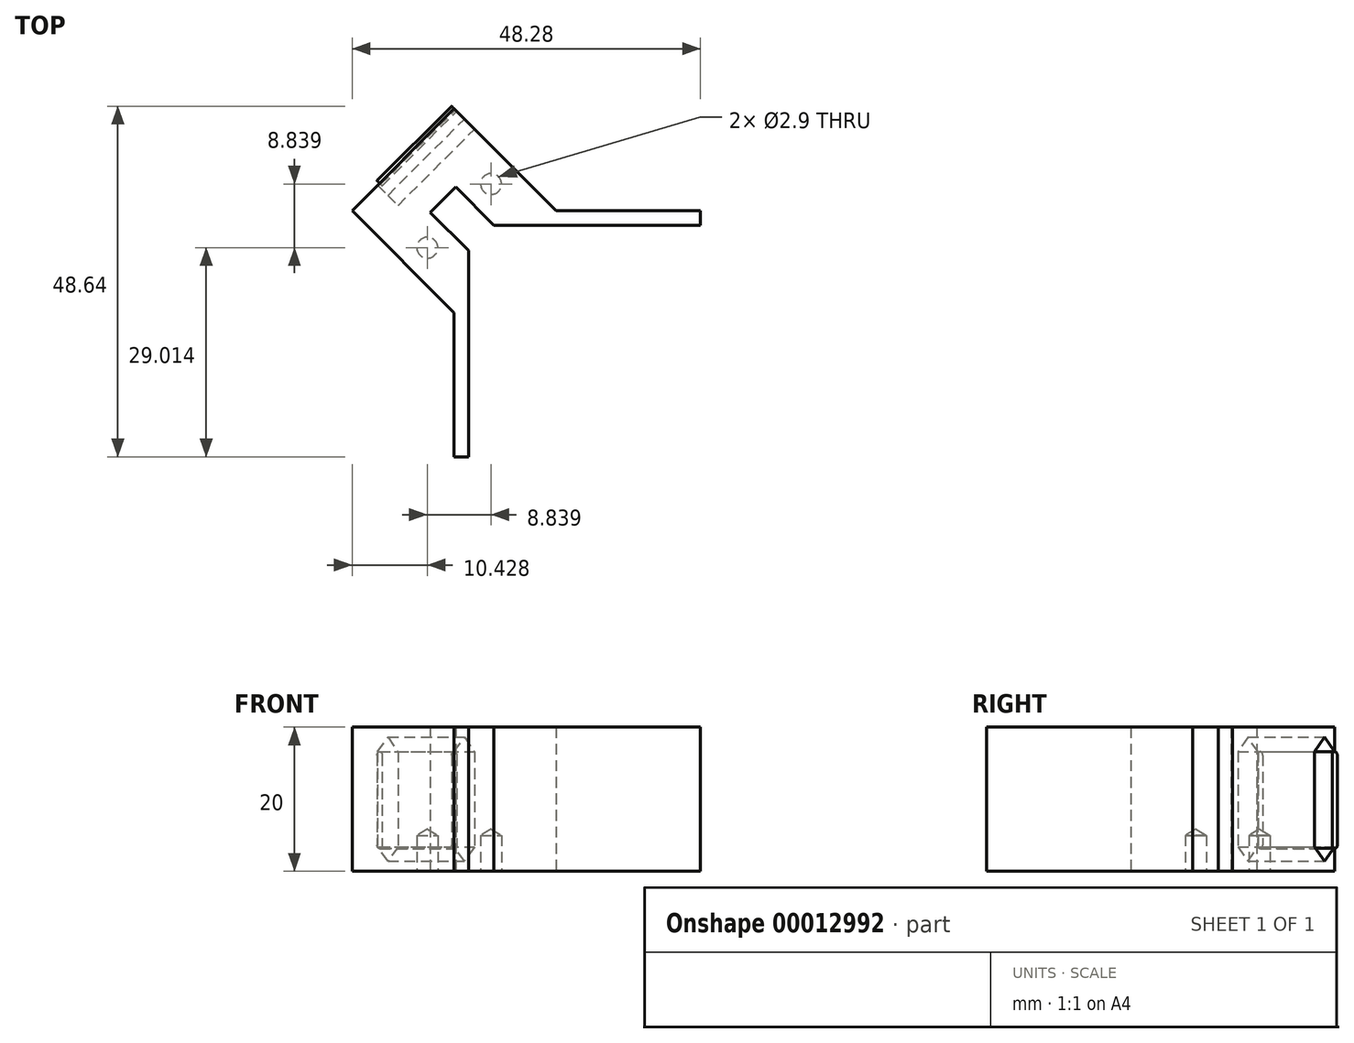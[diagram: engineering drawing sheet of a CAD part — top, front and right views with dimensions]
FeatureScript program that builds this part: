
annotation { "Feature Type Name" : "Feature", "Feature Type Description" : "" }
export const myFeature = defineFeature(function(context is Context, id is Id, definition is map)
    precondition{}
    {
        {
            var Q0;
            Q0=qCreatedBy(makeId("Top.planeOp"),FACE);
            var sketch = newSketch(context, id + "F0", { "sketchPlane" : qUnion([Q0])});
            skLineSegment(sketch, "E0", {"start": v(-14.14, 0) * mm, "end": v(0, -14.14) * mm});
            skLineSegment(sketch, "E1", {"start": v(0, -14.14) * mm, "end": v(0, -34.14) * mm});
            skLineSegment(sketch, "E2", {"start": v(0, -34.14) * mm, "end": v(2, -34.14) * mm});
            skLineSegment(sketch, "E3", {"start": v(2, -34.14) * mm, "end": v(2, -5.54) * mm});
            skLineSegment(sketch, "E4", {"start": v(2, -5.54) * mm, "end": v(-3.3, -0.23) * mm});
            skLineSegment(sketch, "E5", {"start": v(-3.3, -0.23) * mm, "end": v(0.23, 3.3) * mm});
            skLineSegment(sketch, "E6", {"start": v(0.23, 3.3) * mm, "end": v(5.54, -2) * mm});
            skLineSegment(sketch, "E7", {"start": v(5.54, -2) * mm, "end": v(34.14, -2) * mm});
            skLineSegment(sketch, "E8", {"start": v(34.14, -2) * mm, "end": v(34.14, 0) * mm});
            skLineSegment(sketch, "E9", {"start": v(0, 14.14) * mm, "end": v(14.14, 0) * mm});
            skLineSegment(sketch, "E10", {"start": v(14.14, 0) * mm, "end": v(34.14, 0) * mm});
            skLineSegment(sketch, "E11", {"start": v(-14.14, 0) * mm, "end": v(0, 14.14) * mm});
            skSolve(sketch);
        }
        {
            var Q0;
            Q0=makeQuery(id+"F0.imprint","IMPRINT",FACE,{"disambiguationData":[TD([[makeQuery(id+"F0.imprint","IMPRINT",EDGE,{"derivedFrom":sQuery(id+"F0.wireOp",EDGE,"E0")}),1.0]])]});
            extrude(context, id + "F1", {"entities" : qUnion([Q0]), "depth" : 20 * mm});
        }
        {
            var Q0;
            Q0=makeQuery(id+"F1.opExtrude","SWEPT_FACE",FACE,{"disambiguationData":[OSD([sQuery(id+"F0.wireOp",EDGE,"E9")])]});
            var sketch = newSketch(context, id + "F2", { "sketchPlane" : qUnion([Q0])});
            skLineSegment(sketch, "E12.bottom", {"start": v(10, 1.4) * mm, "end": v(6, 1.4) * mm, "construction": true});
            skLineSegment(sketch, "E12.top", {"start": v(10, 18.6) * mm, "end": v(6, 18.6) * mm, "construction": true});
            skLineSegment(sketch, "E12.left", {"start": v(10, 1.4) * mm, "end": v(10, 18.6) * mm, "construction": true});
            skLineSegment(sketch, "E12.right", {"start": v(6, 1.4) * mm, "end": v(6, 18.6) * mm, "construction": true});
            skLineSegment(sketch, "E13", {"start": v(10, 16.6) * mm, "end": v(8, 18.6) * mm});
            skLineSegment(sketch, "E14", {"start": v(8, 18.6) * mm, "end": v(6, 16.6) * mm});
            skLineSegment(sketch, "E15", {"start": v(6, 16.6) * mm, "end": v(6, 3.4) * mm});
            skLineSegment(sketch, "E16", {"start": v(6, 3.4) * mm, "end": v(8, 1.4) * mm});
            skLineSegment(sketch, "E17", {"start": v(8, 1.4) * mm, "end": v(10, 3.4) * mm});
            skLineSegment(sketch, "E18", {"start": v(10, 3.4) * mm, "end": v(10, 16.6) * mm});
            skSolve(sketch);
        }
        {
            var Q0;
            Q0 = qSketchRegion(id + "F2", true);
            extrude(context, id + "F3", {"entities" : qUnion([Q0]), "operationType" : NewBodyOperationType.REMOVE, "oppositeDirection" : true, "depth" : 15 * mm});
        }
        {
            var Q0;
            Q0=makeQuery(id+"F1.opExtrude","SWEPT_FACE",FACE,{"disambiguationData":[OSD([sQuery(id+"F0.wireOp",EDGE,"E9")])]});
            var sketch = newSketch(context, id + "F4", { "sketchPlane" : qUnion([Q0])});
            skLineSegment(sketch, "E19", {"start": v(10, 16.1) * mm, "end": v(10, 3.65) * mm, "construction": true});
            skArc(sketch, "E20.0.startCap", {"start": v(9.5, 16.1) * mm, "mid": v(10, 16.6) * mm, "end": v(10.5, 16.1) * mm});
            skArc(sketch, "E20.0.endCap", {"start": v(10.5, 3.65) * mm, "mid": v(10, 3.15) * mm, "end": v(9.5, 3.65) * mm});
            skLineSegment(sketch, "E20.0.left", {"start": v(10.5, 16.1) * mm, "end": v(10.5, 3.65) * mm});
            skLineSegment(sketch, "E20.0.right", {"start": v(9.5, 16.1) * mm, "end": v(9.5, 3.65) * mm});
            skSolve(sketch);
        }
        {
            var Q0;
            {var subQ1=sQuery(id+"F4.wireOp",EDGE,"E20.0.left");Q0=makeQuery(id+"F4.imprint","IMPRINT",FACE,{"disambiguationData":[TD([[makeQuery(id+"F4.imprint","IMPRINT",EDGE,{"derivedFrom":subQ1}),-1.0]])]});}
            extrude(context, id + "F5", {"entities" : qUnion([Q0]), "oppositeDirection" : true, "depth" : 14.6 * mm});
        }
        {
            var Q0;
            Q0=makeQuery(id+"F1.opExtrude","CAP_FACE",FACE,{"disambiguationData":[OSD([sQuery(id+"F0.wireOp",EDGE,"E0"),sQuery(id+"F0.wireOp",EDGE,"E1"),sQuery(id+"F0.wireOp",EDGE,"E2"),sQuery(id+"F0.wireOp",EDGE,"E3"),sQuery(id+"F0.wireOp",EDGE,"E4"),sQuery(id+"F0.wireOp",EDGE,"E5"),sQuery(id+"F0.wireOp",EDGE,"E6"),sQuery(id+"F0.wireOp",EDGE,"E7"),sQuery(id+"F0.wireOp",EDGE,"E8"),sQuery(id+"F0.wireOp",EDGE,"E9"),sQuery(id+"F0.wireOp",EDGE,"E10"),sQuery(id+"F0.wireOp",EDGE,"E11")])],"isStart":true});
            var sketch = newSketch(context, id + "F6", { "sketchPlane" : qUnion([Q0])});
            skLineSegment(sketch, "E21", {"start": v(-11.5, -2.65) * mm, "end": v(0, 8.84) * mm, "construction": true});
            skPoint(sketch, "E22", {"position": v(-3.71, 5.13) * mm});
            skPoint(sketch, "E23", {"position": v(5.13, -3.71) * mm});
            skSolve(sketch);
        }
        {
            var Q0;
            Q0=sQuery(id+"F6.wireOp",VERTEX,"E22");
            var Q1;
            Q1=sQuery(id+"F6.wireOp",VERTEX,"E23");
            var Q2;
            Q2=makeQuery(id+"F1.opExtrude","SWEPT_BODY",BODY,{"disambiguationData":[OSD([sQuery(id+"F0.wireOp",EDGE,"E0"),sQuery(id+"F0.wireOp",EDGE,"E1"),sQuery(id+"F0.wireOp",EDGE,"E2"),sQuery(id+"F0.wireOp",EDGE,"E3"),sQuery(id+"F0.wireOp",EDGE,"E4"),sQuery(id+"F0.wireOp",EDGE,"E5"),sQuery(id+"F0.wireOp",EDGE,"E6"),sQuery(id+"F0.wireOp",EDGE,"E7"),sQuery(id+"F0.wireOp",EDGE,"E8"),sQuery(id+"F0.wireOp",EDGE,"E9"),sQuery(id+"F0.wireOp",EDGE,"E10"),sQuery(id+"F0.wireOp",EDGE,"E11")])]});
            hole(context, id + "F7", {"style" : HoleStyle.SIMPLE, "holeDiameter" : 2.9 * mm, "endStyle" : HoleEndStyle.BLIND, "holeDepth" : 5 * mm, "locations" : qUnion([Q0, Q1]), "scope" : qUnion([Q2])});
        }
    });
